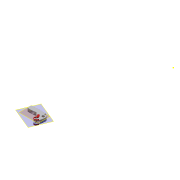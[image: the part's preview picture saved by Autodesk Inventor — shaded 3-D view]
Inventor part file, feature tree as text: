
AUTODESK INVENTOR PART (.ipt)
format: ipt  version: 2016 (Build 200138000, 138)  size: 786,432 bytes
history: native  units: in
note: dims shown in document units (in); Inventor stores cm internally (conversion verified against a paired STEP export)
features: extrude x3, fillet x3, sketch x3, plane x2, projected_geometry x2, other x1, mirror x1, imported_body x1
ambient origin geometry x8: Origin, YZ Plane, XZ Plane, XY Plane, X Axis, Y Axis, Z Axis, Center Point
bodies: Solid1 (feature_tree), Solid2 (feature_tree)
feature tree (16):
  other  "033-fe_lever-0425_stp.ipt1"
  plane  "Work Plane1"
  extrude  "Extrusion1"  Depth=0.0512in
  fillet  "Fillet1"  Radius=0.1378in
  plane  "Work Plane2"
  mirror  "Mirror1"
  extrude  "Extrusion2"  Depth=0.0787in TaperAngle=0.0deg
  fillet  "Fillet2"  Radius=0.0787in
  extrude  "Extrusion3"  Depth=0.0787in TaperAngle=0.0deg
  fillet  "Fillet3"  Radius=0.0394in
  imported_body  "Base1"
  sketch  "Sketch1"  dims[d0=-0.0787in d1=0.0512in d2=0.1378in d3=0.0in]
  sketch  "Sketch3"  dims[d4=0.0217in d5=0.0787in d6=0.0in d7=0.0787in]
  sketch  "Sketch7"  dims[d9=0.0315in d10=0.0787in d11=0.0in d12=0.0394in]
  projected_geometry  "Projected Loop3"
  projected_geometry  "Project Cut Edges1"
